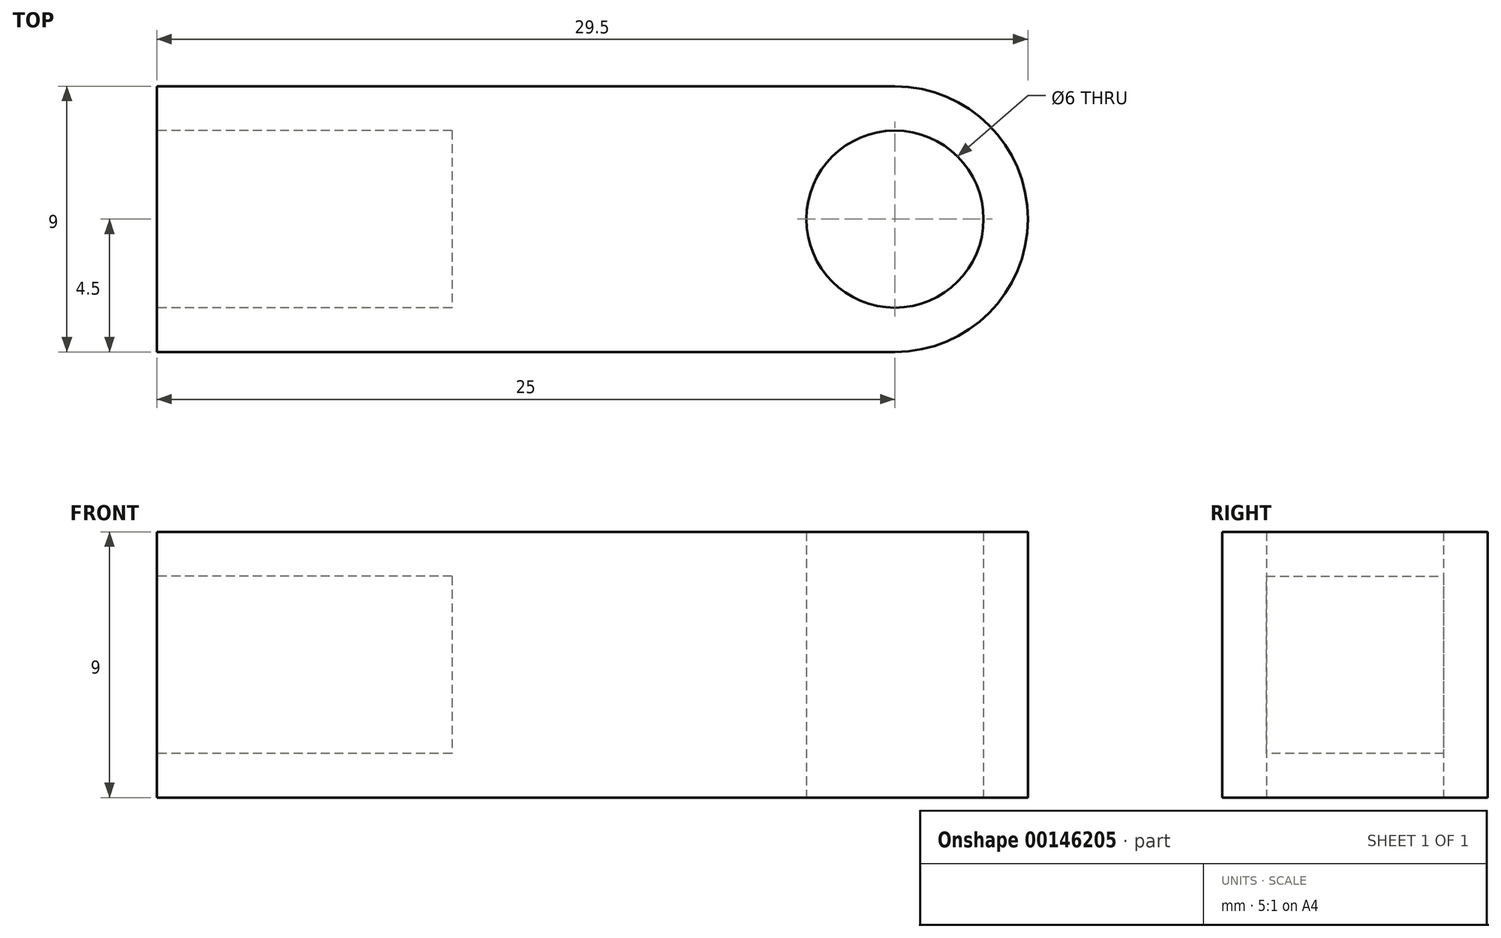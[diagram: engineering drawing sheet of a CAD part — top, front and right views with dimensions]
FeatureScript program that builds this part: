
annotation { "Feature Type Name" : "Feature", "Feature Type Description" : "" }
export const myFeature = defineFeature(function(context is Context, id is Id, definition is map)
    precondition{}
    {
        {
            var Q0;
            Q0=qCreatedBy(makeId("Top.planeOp"),FACE);
            var sketch = newSketch(context, id + "F0", { "sketchPlane" : qUnion([Q0])});
            skArc(sketch, "E0", {"start": v(0, -4.5) * mm, "mid": v(4.5, 0) * mm, "end": v(0, 4.5) * mm});
            skLineSegment(sketch, "E1", {"start": v(0, 0) * mm, "end": v(-25, 0) * mm});
            skLineSegment(sketch, "E2.bottom", {"start": v(-25, 4.5) * mm, "end": v(0, 4.5) * mm});
            skLineSegment(sketch, "E2.top", {"start": v(-25, -4.5) * mm, "end": v(0, -4.5) * mm});
            skLineSegment(sketch, "E3", {"start": v(-25, 4.5) * mm, "end": v(-25, -4.5) * mm});
            skCircle(sketch, "E4.0", {"center": v(0, 0) * mm, "radius": 3 * mm});
            skSolve(sketch);
        }
        {
            var Q0;
            Q0=makeQuery(id+"F0.imprint","IMPRINT",FACE,{"disambiguationData":[TD([[makeQuery(id+"F0.imprint","IMPRINT",EDGE,{"derivedFrom":sQuery(id+"F0.wireOp",EDGE,"i2H6iiVw-H3aJ-6FKV-5UGR-f3UhmpoqAZ2u")}),-1.0]])]});
            var Q1;
            Q1=makeQuery(id+"F0.imprint","IMPRINT",FACE,{"disambiguationData":[TD([[makeQuery(id+"F0.imprint","IMPRINT",EDGE,{"derivedFrom":sQuery(id+"F0.wireOp",EDGE,"E0")}),1.0]])]});
            extrude(context, id + "F1", {"entities" : qUnion([Q0, Q1]), "depth" : 9 * mm});
        }
        {
            var Q0;
            Q0=makeQuery(id+"F1.opExtrude","SWEPT_FACE",FACE,{"disambiguationData":[OSD([sQuery(id+"F0.wireOp",EDGE,"E3")])]});
            var sketch = newSketch(context, id + "F2", { "sketchPlane" : qUnion([Q0])});
            skLineSegment(sketch, "E5.0", {"start": v(-3, 1.5) * mm, "end": v(3, 1.5) * mm});
            skLineSegment(sketch, "E5.1", {"start": v(-3, 7.5) * mm, "end": v(-3, 1.5) * mm});
            skLineSegment(sketch, "E5.2", {"start": v(3, 7.5) * mm, "end": v(-3, 7.5) * mm});
            skLineSegment(sketch, "E5.3", {"start": v(3, 1.5) * mm, "end": v(3, 7.5) * mm});
            skSolve(sketch);
        }
        {
            var Q0;
            Q0=makeQuery(id+"F2.imprint","IMPRINT",FACE,{"disambiguationData":[TD([[makeQuery(id+"F2.imprint","IMPRINT",EDGE,{"derivedFrom":sQuery(id+"F2.wireOp",EDGE,"E5.0")}),1.0]])]});
            extrude(context, id + "F3", {"entities" : qUnion([Q0]), "operationType" : NewBodyOperationType.REMOVE, "oppositeDirection" : true, "depth" : 10 * mm});
        }
    });
